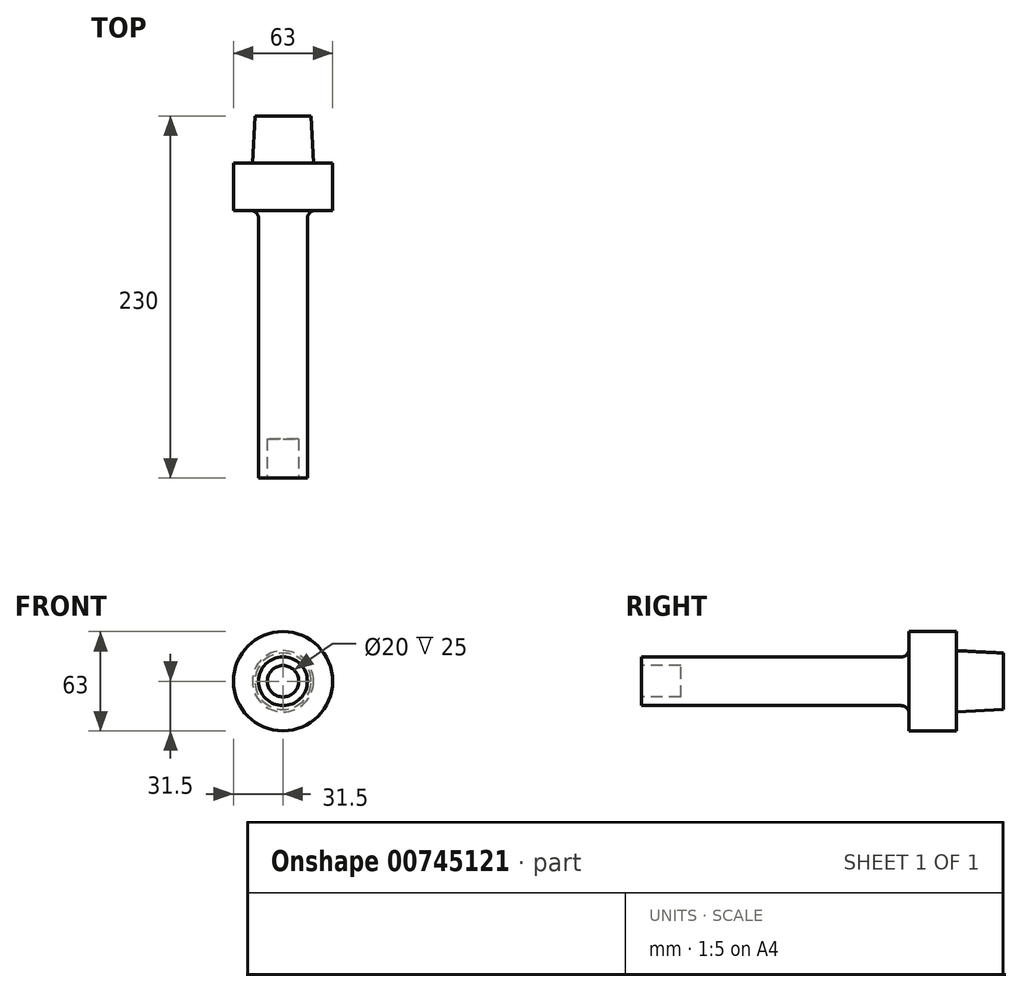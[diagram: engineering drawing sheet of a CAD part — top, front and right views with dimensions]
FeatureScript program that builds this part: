
annotation { "Feature Type Name" : "Feature", "Feature Type Description" : "" }
export const myFeature = defineFeature(function(context is Context, id is Id, definition is map)
    precondition{}
    {
        {
            var Q0;
            Q0=qCreatedBy(makeId("Front.planeOp"),FACE);
            var sketch = newSketch(context, id + "F0", { "sketchPlane" : qUnion([Q0])});
            skCircle(sketch, "E0", {"center": v(0, 0) * mm, "radius": 31.5 * mm});
            skSolve(sketch);
        }
        {
            var Q0;
            Q0 = qSketchRegion(id + "F0", true);
            extrude(context, id + "F1", {"entities" : qUnion([Q0]), "depth" : 200 * mm, "offsetDistance" : 25 * mm});
        }
        {
            var Q0;
            Q0=makeQuery(id+"F1.opExtrude","CAP_FACE",FACE,{"disambiguationData":[OSD([sQuery(id+"F0.wireOp",EDGE,"E0")])],"isStart":false});
            var sketch = newSketch(context, id + "F2", { "sketchPlane" : qUnion([Q0])});
            skCircle(sketch, "E1", {"center": v(0, 0) * mm, "radius": 15.5 * mm});
            skCircle(sketch, "E2", {"center": v(0, 0) * mm, "radius": 49.46 * mm});
            skSolve(sketch);
        }
        {
            var Q0;
            Q0 = qSketchRegion(id + "F2", true);
            extrude(context, id + "F3", {"entities" : qUnion([Q0]), "operationType" : NewBodyOperationType.REMOVE, "oppositeDirection" : true, "depth" : 170 * mm, "offsetDistance" : 25 * mm});
        }
        {
            var Q0;
            Q0=makeQuery(id+"F3.boolean.opBoolean","COPY",EDGE,{"derivedFrom":makeQuery(id+"F3.opExtrude","CAP_EDGE",EDGE,{"disambiguationData":[OSD([sQuery(id+"F2.wireOp",EDGE,"E1")])],"isStart":false})});
            fillet(context, id + "F4", {"entities" : qUnion([Q0]), "radius" : 5 * mm, "tangentPropagation" : true, "allowEdgeOverflow" : false});
        }
        {
            var Q0;
            Q0=makeQuery(id+"F1.opExtrude","CAP_FACE",FACE,{"disambiguationData":[OSD([sQuery(id+"F0.wireOp",EDGE,"E0")])],"isStart":true});
            var sketch = newSketch(context, id + "F5", { "sketchPlane" : qUnion([Q0])});
            skCircle(sketch, "E3", {"center": v(0, 0) * mm, "radius": 19.47 * mm});
            skSolve(sketch);
        }
        {
            var Q0;
            Q0 = qSketchRegion(id + "F5", true);
            extrude(context, id + "F6", {"entities" : qUnion([Q0]), "operationType" : NewBodyOperationType.ADD, "depth" : 30 * mm, "offsetDistance" : 25 * mm, "hasDraft" : true, "draftAngle" : 3 * degree, "draftPullDirection" : true});
        }
        {
            var Q0;
            Q0=makeQuery(id+"F1.opExtrude","CAP_FACE",FACE,{"disambiguationData":[OSD([sQuery(id+"F0.wireOp",EDGE,"E0")])],"isStart":false});
            var sketch = newSketch(context, id + "F7", { "sketchPlane" : qUnion([Q0])});
            skCircle(sketch, "E4", {"center": v(0, 0) * mm, "radius": 10 * mm});
            skSolve(sketch);
        }
        {
            var Q0;
            Q0 = qSketchRegion(id + "F7", true);
            extrude(context, id + "F8", {"entities" : qUnion([Q0]), "operationType" : NewBodyOperationType.REMOVE, "oppositeDirection" : true, "depth" : 25 * mm, "offsetDistance" : 25 * mm});
        }
    });
